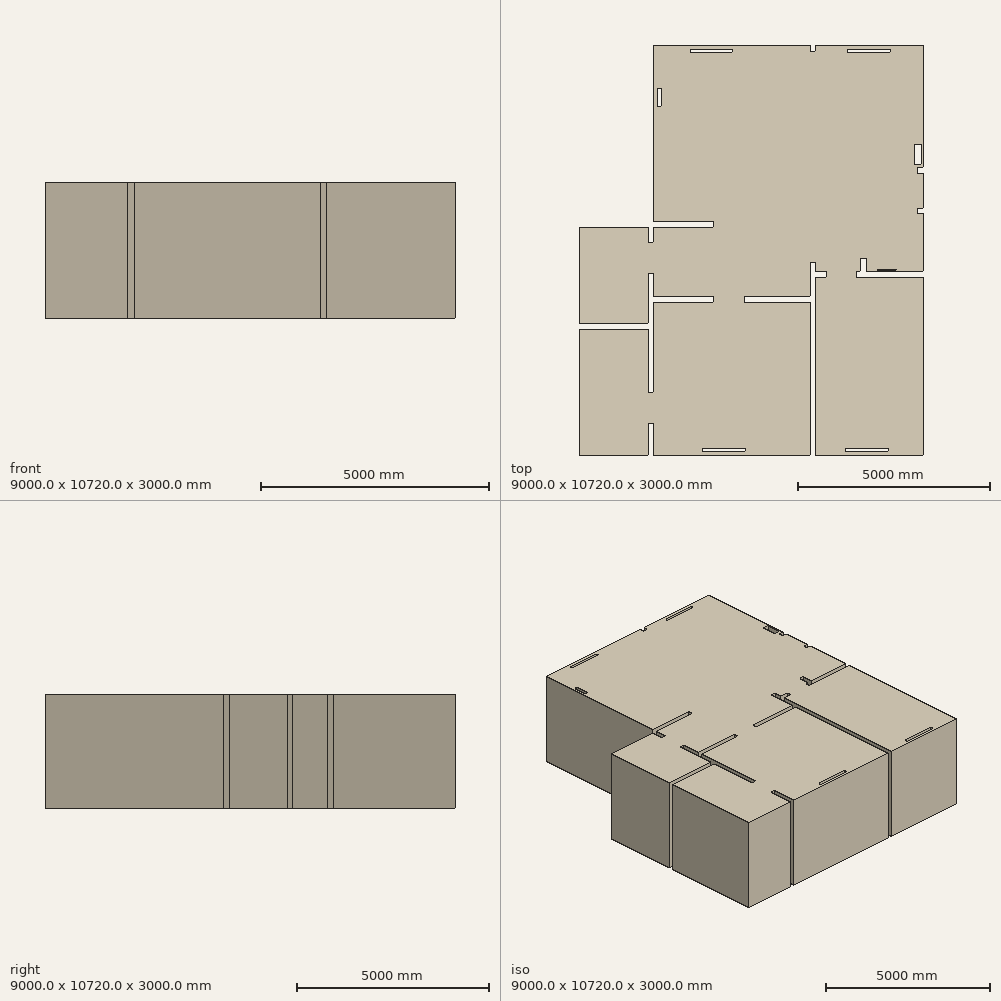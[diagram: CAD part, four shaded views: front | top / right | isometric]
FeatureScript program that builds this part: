
annotation { "Feature Type Name" : "Feature", "Feature Type Description" : "" }
export const myFeature = defineFeature(function(context is Context, id is Id, definition is map)
    precondition{}
    {
        {
            var Q0;
            Q0=qCreatedBy(makeId("Top.planeOp"),FACE);
            var sketch = newSketch(context, id + "F0", { "sketchPlane" : qUnion([Q0])});
            skLineSegment(sketch, "E0", {"start": v(-2362.56, 0) * mm, "end": v(-2362.56, 4600) * mm});
            skLineSegment(sketch, "E1", {"start": v(1717.44, 4600) * mm, "end": v(1717.44, 0) * mm});
            skLineSegment(sketch, "E2", {"start": v(1717.44, 0) * mm, "end": v(0, 0) * mm});
            skLineSegment(sketch, "E3", {"start": v(0, 0) * mm, "end": v(0, -150) * mm});
            skLineSegment(sketch, "E4", {"start": v(0, -150) * mm, "end": v(1717.44, -150) * mm});
            skLineSegment(sketch, "E5", {"start": v(1867.44, 4600) * mm, "end": v(4687.44, 4600) * mm});
            skLineSegment(sketch, "E6", {"start": v(4687.44, 4600) * mm, "end": v(4687.44, 1400) * mm});
            skLineSegment(sketch, "E7", {"start": v(4687.44, 1400) * mm, "end": v(2942.79, 1400) * mm});
            skLineSegment(sketch, "E8", {"start": v(2942.79, 1400) * mm, "end": v(2942.79, 1250) * mm});
            skLineSegment(sketch, "E9", {"start": v(2942.79, -1320) * mm, "end": v(2942.79, -1470) * mm});
            skLineSegment(sketch, "E10", {"start": v(2942.79, -1470) * mm, "end": v(4678.78, -1470) * mm});
            skLineSegment(sketch, "E11", {"start": v(4678.78, -1470) * mm, "end": v(4678.78, -6120) * mm});
            skLineSegment(sketch, "E12", {"start": v(4678.78, -6120) * mm, "end": v(1858.78, -6120) * mm});
            skLineSegment(sketch, "E13", {"start": v(1858.78, -6120) * mm, "end": v(1858.78, -1470) * mm});
            skLineSegment(sketch, "E14", {"start": v(1867.44, -1320) * mm, "end": v(1867.44, -1075.1) * mm});
            skLineSegment(sketch, "E15", {"start": v(1867.44, -1075.1) * mm, "end": v(1717.44, -1075.1) * mm});
            skLineSegment(sketch, "E16", {"start": v(1717.44, -1075.1) * mm, "end": v(1717.44, -1970) * mm});
            skLineSegment(sketch, "E17", {"start": v(1717.44, -1970) * mm, "end": v(0, -1970) * mm});
            skLineSegment(sketch, "E18", {"start": v(0, -1970) * mm, "end": v(0, -2120) * mm});
            skLineSegment(sketch, "E19", {"start": v(0, -2120) * mm, "end": v(1717.44, -2120) * mm});
            skLineSegment(sketch, "E20", {"start": v(1717.44, -2120) * mm, "end": v(1717.44, -6120) * mm});
            skLineSegment(sketch, "E21", {"start": v(1717.44, -6120) * mm, "end": v(-2362.56, -6120) * mm});
            skLineSegment(sketch, "E22", {"start": v(-2362.56, -6120) * mm, "end": v(-2362.56, -5274.16) * mm});
            skLineSegment(sketch, "E23", {"start": v(-2362.56, -4474.16) * mm, "end": v(-2362.56, -2120) * mm});
            skLineSegment(sketch, "E24", {"start": v(-2362.56, -2120) * mm, "end": v(-800, -2120) * mm});
            skLineSegment(sketch, "E25", {"start": v(-800, -2120) * mm, "end": v(-800, -1970) * mm});
            skLineSegment(sketch, "E26", {"start": v(-800, -1970) * mm, "end": v(-2362.56, -1970) * mm});
            skLineSegment(sketch, "E27", {"start": v(-2362.56, 0) * mm, "end": v(-800, 0) * mm});
            skLineSegment(sketch, "E28", {"start": v(-800, 0) * mm, "end": v(-800, -150) * mm});
            skLineSegment(sketch, "E29", {"start": v(-800, -150) * mm, "end": v(-2362.56, -150) * mm});
            skLineSegment(sketch, "E30", {"start": v(-2362.56, -150) * mm, "end": v(-2362.56, -556.06) * mm});
            skLineSegment(sketch, "E31", {"start": v(-2362.56, -556.06) * mm, "end": v(-2512.56, -556.06) * mm});
            skLineSegment(sketch, "E32", {"start": v(-2512.56, -556.06) * mm, "end": v(-2512.56, -150) * mm});
            skLineSegment(sketch, "E33", {"start": v(1867.44, -275.1) * mm, "end": v(1867.44, 1250) * mm});
            skLineSegment(sketch, "E34", {"start": v(1867.44, 1250) * mm, "end": v(2142.79, 1250) * mm});
            skLineSegment(sketch, "E35", {"start": v(2142.79, 1250) * mm, "end": v(2142.79, 1400) * mm});
            skLineSegment(sketch, "E36", {"start": v(2142.79, 1400) * mm, "end": v(1867.44, 1400) * mm});
            skLineSegment(sketch, "E37", {"start": v(1867.44, 1400) * mm, "end": v(1867.44, 4600) * mm});
            skLineSegment(sketch, "E38", {"start": v(-2362.56, -1970) * mm, "end": v(-2362.56, -1356.06) * mm});
            skLineSegment(sketch, "E39", {"start": v(-2362.56, -1356.06) * mm, "end": v(-2512.56, -1356.06) * mm});
            skLineSegment(sketch, "E40", {"start": v(-2512.56, -1356.06) * mm, "end": v(-2512.56, -2670) * mm});
            skLineSegment(sketch, "E41", {"start": v(-2512.56, -2670) * mm, "end": v(-4312.56, -2670) * mm});
            skLineSegment(sketch, "E42", {"start": v(2142.79, -1320) * mm, "end": v(2142.79, -1470) * mm});
            skLineSegment(sketch, "E43", {"start": v(1867.44, -1320) * mm, "end": v(2142.79, -1320) * mm});
            skLineSegment(sketch, "E44", {"start": v(1858.78, -1470) * mm, "end": v(2142.79, -1470) * mm});
            skLineSegment(sketch, "E45", {"start": v(-2362.56, -5274.16) * mm, "end": v(-2512.56, -5274.16) * mm});
            skLineSegment(sketch, "E46", {"start": v(-2512.56, -5274.16) * mm, "end": v(-2512.56, -6120) * mm});
            skLineSegment(sketch, "E47", {"start": v(-2512.56, -6120) * mm, "end": v(-4312.56, -6120) * mm});
            skLineSegment(sketch, "E48", {"start": v(-4312.56, -6120) * mm, "end": v(-4312.56, -2820) * mm});
            skLineSegment(sketch, "E49", {"start": v(-4312.56, -2820) * mm, "end": v(-2512.56, -2820) * mm});
            skLineSegment(sketch, "E50", {"start": v(-2512.56, -2820) * mm, "end": v(-2512.56, -4474.16) * mm});
            skLineSegment(sketch, "E51", {"start": v(-2512.56, -4474.16) * mm, "end": v(-2362.56, -4474.16) * mm});
            skLineSegment(sketch, "E52", {"start": v(3043.18, 1250) * mm, "end": v(3043.18, 1151.46) * mm});
            skLineSegment(sketch, "E53", {"start": v(3043.18, 1151.46) * mm, "end": v(3193.18, 1151.46) * mm});
            skLineSegment(sketch, "E54", {"start": v(3193.18, 1151.46) * mm, "end": v(3193.18, 1250) * mm});
            skLineSegment(sketch, "E55", {"start": v(2942.79, 1250) * mm, "end": v(3043.18, 1250) * mm});
            skLineSegment(sketch, "E56", {"start": v(3193.18, 1250) * mm, "end": v(4687.44, 1250) * mm});
            skLineSegment(sketch, "E57", {"start": v(3043.18, 551.46) * mm, "end": v(3193.18, 551.46) * mm});
            skLineSegment(sketch, "E58", {"start": v(3193.18, 551.46) * mm, "end": v(3193.18, 350) * mm});
            skLineSegment(sketch, "E59", {"start": v(3193.18, 350) * mm, "end": v(4687.44, 350) * mm});
            skLineSegment(sketch, "E60", {"start": v(3043.18, 551.46) * mm, "end": v(3043.18, -369.05) * mm});
            skLineSegment(sketch, "E61", {"start": v(3043.18, -369.05) * mm, "end": v(3193.18, -369.05) * mm});
            skLineSegment(sketch, "E62", {"start": v(3193.18, -369.05) * mm, "end": v(3193.18, 200) * mm});
            skLineSegment(sketch, "E63", {"start": v(3193.18, 200) * mm, "end": v(4678.78, 200) * mm});
            skLineSegment(sketch, "E64", {"start": v(4687.44, 350) * mm, "end": v(4687.44, 1250) * mm});
            skLineSegment(sketch, "E65", {"start": v(3043.18, -969.05) * mm, "end": v(3193.18, -969.05) * mm});
            skLineSegment(sketch, "E66", {"start": v(3193.18, -969.05) * mm, "end": v(3193.18, -1320) * mm});
            skLineSegment(sketch, "E67", {"start": v(3043.18, -969.05) * mm, "end": v(3043.18, -1320) * mm});
            skLineSegment(sketch, "E68", {"start": v(4678.78, -1320) * mm, "end": v(4678.78, 200) * mm});
            skLineSegment(sketch, "E69", {"start": v(2942.79, -1320) * mm, "end": v(3043.18, -1320) * mm});
            skLineSegment(sketch, "E70", {"start": v(3193.18, -1320) * mm, "end": v(4678.78, -1320) * mm});
            skLineSegment(sketch, "E71", {"start": v(1717.44, -150) * mm, "end": v(1717.44, -275.75) * mm});
            skLineSegment(sketch, "E72", {"start": v(1867.44, -275.1) * mm, "end": v(1717.44, -275.1) * mm});
            skLineSegment(sketch, "E73", {"start": v(-4312.56, -2670) * mm, "end": v(-4312.56, -150) * mm});
            skLineSegment(sketch, "E74", {"start": v(-4312.56, -150) * mm, "end": v(-2512.56, -150) * mm});
            skLineSegment(sketch, "E75", {"start": v(-2362.56, 4600) * mm, "end": v(1717.44, 4600) * mm});
            skLineSegment(sketch, "E76", {"start": v(2942.79, 1400) * mm, "end": v(3350, 1400) * mm});
            skLineSegment(sketch, "E77", {"start": v(3350, 1400) * mm, "end": v(3450, 1400) * mm});
            skLineSegment(sketch, "E78", {"start": v(3450, 1250) * mm, "end": v(4050, 1250) * mm});
            skLineSegment(sketch, "E79", {"start": v(4050, 1250) * mm, "end": v(4149.99, 1251.57) * mm});
            skLineSegment(sketch, "E80", {"start": v(3450, 200) * mm, "end": v(4050, 200) * mm});
            skLineSegment(sketch, "E81", {"start": v(4050, 200) * mm, "end": v(4150, 200) * mm});
            skLineSegment(sketch, "E82.bottom", {"start": v(2699.43, 4500) * mm, "end": v(3819.43, 4500) * mm});
            skLineSegment(sketch, "E82.top", {"start": v(2699.43, 4405) * mm, "end": v(3819.43, 4405) * mm});
            skLineSegment(sketch, "E82.left", {"start": v(2699.43, 4500) * mm, "end": v(2699.43, 4405) * mm});
            skLineSegment(sketch, "E82.right", {"start": v(3819.43, 4500) * mm, "end": v(3819.43, 4405) * mm});
            skLineSegment(sketch, "E83.bottom", {"start": v(-1420, 4500) * mm, "end": v(-300, 4500) * mm});
            skLineSegment(sketch, "E83.top", {"start": v(-1420, 4405) * mm, "end": v(-300, 4405) * mm});
            skLineSegment(sketch, "E83.left", {"start": v(-1420, 4500) * mm, "end": v(-1420, 4405) * mm});
            skLineSegment(sketch, "E83.right", {"start": v(-300, 4500) * mm, "end": v(-300, 4405) * mm});
            skLineSegment(sketch, "E84.bottom", {"start": v(-2262.56, 3480) * mm, "end": v(-2167.56, 3480) * mm});
            skLineSegment(sketch, "E84.top", {"start": v(-2262.56, 3000) * mm, "end": v(-2167.56, 3000) * mm});
            skLineSegment(sketch, "E84.left", {"start": v(-2262.56, 3480) * mm, "end": v(-2262.56, 3000) * mm});
            skLineSegment(sketch, "E84.right", {"start": v(-2167.56, 3480) * mm, "end": v(-2167.56, 3000) * mm});
            skLineSegment(sketch, "E85.bottom", {"start": v(4437.44, 2000) * mm, "end": v(4637.44, 2000) * mm});
            skLineSegment(sketch, "E85.top", {"start": v(4437.44, 1500) * mm, "end": v(4637.44, 1500) * mm});
            skLineSegment(sketch, "E85.left", {"start": v(4437.44, 2000) * mm, "end": v(4437.44, 1500) * mm});
            skLineSegment(sketch, "E85.right", {"start": v(4637.44, 2000) * mm, "end": v(4637.44, 1500) * mm});
            skLineSegment(sketch, "E86", {"start": v(4537.44, 1750) * mm, "end": v(4537.44, 2000) * mm});
            skPoint(sketch, "E86.startSnap0", {"position": v(4637.44, 1750) * mm});
            skPoint(sketch, "E86.startSnap1", {"position": v(4537.44, 2000) * mm});
            skLineSegment(sketch, "E87", {"start": v(4537.44, 1750) * mm, "end": v(4537.44, 1500) * mm});
            skLineSegment(sketch, "E88", {"start": v(4537.44, 1750) * mm, "end": v(4437.44, 1750) * mm});
            skLineSegment(sketch, "E89", {"start": v(4537.44, 1750) * mm, "end": v(4637.44, 1750) * mm});
            skLineSegment(sketch, "E90", {"start": v(4537.44, 1750) * mm, "end": v(4537.44, 1800) * mm});
            skLineSegment(sketch, "E91", {"start": v(4537.44, 1750) * mm, "end": v(4537.44, 1700) * mm});
            skLineSegment(sketch, "E92", {"start": v(4537.44, 1800) * mm, "end": v(4537.44, 4452.5) * mm});
            skPoint(sketch, "E92.endSnap0", {"position": v(3819.43, 4452.5) * mm});
            skLineSegment(sketch, "E93", {"start": v(4537.44, 4452.5) * mm, "end": v(3819.43, 4452.5) * mm});
            skLineSegment(sketch, "E94", {"start": v(3819.43, 4452.5) * mm, "end": v(-300, 4452.5) * mm});
            skLineSegment(sketch, "E95", {"start": v(-300, 4452.5) * mm, "end": v(-2215.06, 4452.5) * mm});
            skPoint(sketch, "E95.endSnap0", {"position": v(-2215.06, 3480) * mm});
            skLineSegment(sketch, "E96", {"start": v(-2215.06, 4452.5) * mm, "end": v(-2215.06, 3480) * mm});
            skLineSegment(sketch, "E97.bottom", {"start": v(2647, -5925) * mm, "end": v(3767, -5925) * mm});
            skLineSegment(sketch, "E97.top", {"start": v(2647, -6020) * mm, "end": v(3767, -6020) * mm});
            skLineSegment(sketch, "E97.left", {"start": v(2647, -5925) * mm, "end": v(2647, -6020) * mm});
            skLineSegment(sketch, "E97.right", {"start": v(3767, -5925) * mm, "end": v(3767, -6020) * mm});
            skLineSegment(sketch, "E98.bottom", {"start": v(-1099.84, -5925) * mm, "end": v(20.16, -5925) * mm});
            skLineSegment(sketch, "E98.top", {"start": v(-1099.84, -6020) * mm, "end": v(20.16, -6020) * mm});
            skLineSegment(sketch, "E98.left", {"start": v(-1099.84, -5925) * mm, "end": v(-1099.84, -6020) * mm});
            skLineSegment(sketch, "E98.right", {"start": v(20.16, -5925) * mm, "end": v(20.16, -6020) * mm});
            skLineSegment(sketch, "E99.bottom", {"start": v(3484.05, -1255) * mm, "end": v(3984.05, -1255) * mm});
            skLineSegment(sketch, "E99.top", {"start": v(3484.05, -1270) * mm, "end": v(3984.05, -1270) * mm});
            skLineSegment(sketch, "E99.left", {"start": v(3484.05, -1255) * mm, "end": v(3484.05, -1270) * mm});
            skLineSegment(sketch, "E99.right", {"start": v(3984.05, -1255) * mm, "end": v(3984.05, -1270) * mm});
            skLineSegment(sketch, "E100", {"start": v(4537.44, 1800) * mm, "end": v(4537.44, -1255) * mm});
            skLineSegment(sketch, "E101", {"start": v(4537.44, -1255) * mm, "end": v(3984.05, -1262.5) * mm});
            skSolve(sketch);
        }
        {
            var Q0;
            Q0 = qSketchRegion(id + "F0", true);
            extrude(context, id + "F1", {"entities" : qUnion([Q0]), "depth" : 3000 * mm});
        }
    });
